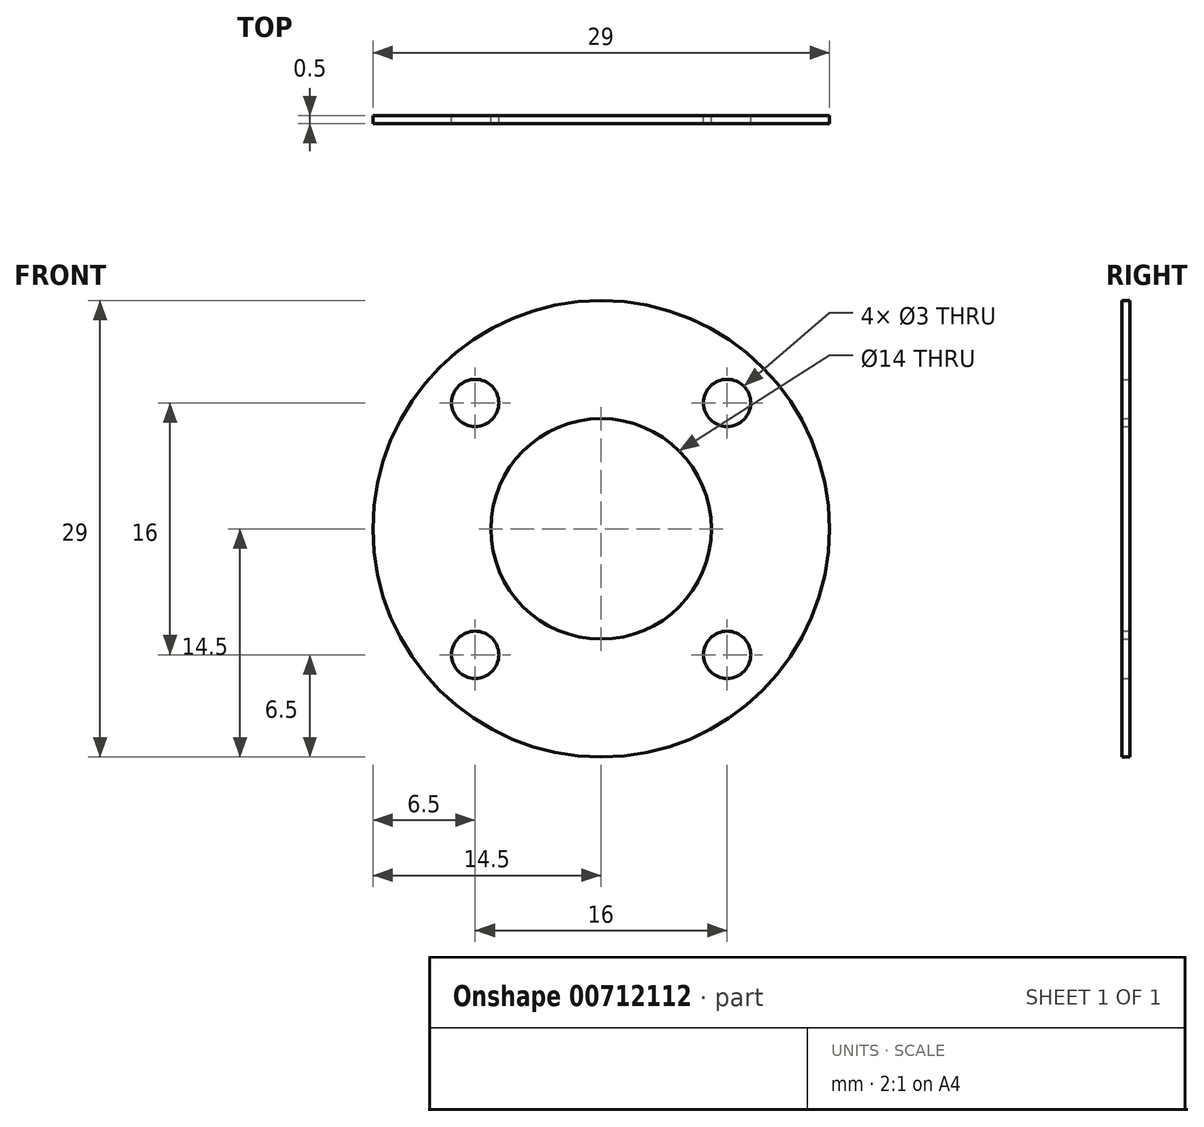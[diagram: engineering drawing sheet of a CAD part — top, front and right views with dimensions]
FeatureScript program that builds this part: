
annotation { "Feature Type Name" : "Feature", "Feature Type Description" : "" }
export const myFeature = defineFeature(function(context is Context, id is Id, definition is map)
    precondition{}
    {
        {
            var Q0;
            Q0=qCreatedBy(makeId("Front.planeOp"),FACE);
            var sketch = newSketch(context, id + "F0", { "sketchPlane" : qUnion([Q0])});
            skCircle(sketch, "E0", {"center": v(0, 0) * mm, "radius": 14.5 * mm});
            skCircle(sketch, "E1", {"center": v(0, 0) * mm, "radius": 7 * mm});
            skLineSegment(sketch, "E2", {"start": v(0, 36.08) * mm, "end": v(0, -28.1) * mm, "construction": true});
            skLineSegment(sketch, "E3", {"start": v(-24.29, 0) * mm, "end": v(25.23, 0) * mm, "construction": true});
            skLineSegment(sketch, "E4.0", {"start": v(-8, 36.08) * mm, "end": v(-8, -28.1) * mm, "construction": true});
            skLineSegment(sketch, "E5.0", {"start": v(-24.29, 8) * mm, "end": v(25.23, 8) * mm, "construction": true});
            skLineSegment(sketch, "E6.MirrorCS", {"start": v(8, 36.08) * mm, "end": v(8, -28.1) * mm, "construction": true});
            skLineSegment(sketch, "E7.MirrorCS", {"start": v(-24.29, -8) * mm, "end": v(25.23, -8) * mm, "construction": true});
            skCircle(sketch, "E8", {"center": v(-8, 8) * mm, "radius": 1.5 * mm});
            skCircle(sketch, "E9", {"center": v(8, 8) * mm, "radius": 1.5 * mm});
            skCircle(sketch, "E10", {"center": v(-8, -8) * mm, "radius": 1.5 * mm});
            skCircle(sketch, "E11", {"center": v(8, -8) * mm, "radius": 1.5 * mm});
            skSolve(sketch);
        }
        {
            var Q0;
            Q0=makeQuery(id+"F0.imprint","IMPRINT",FACE,{"disambiguationData":[TD([[makeQuery(id+"F0.imprint","IMPRINT",EDGE,{"derivedFrom":sQuery(id+"F0.wireOp",EDGE,"E0")}),1.0]])]});
            extrude(context, id + "F1", {"entities" : qUnion([Q0]), "depth" : .5 * mm, "offsetDistance" : 25 * mm});
        }
    });
